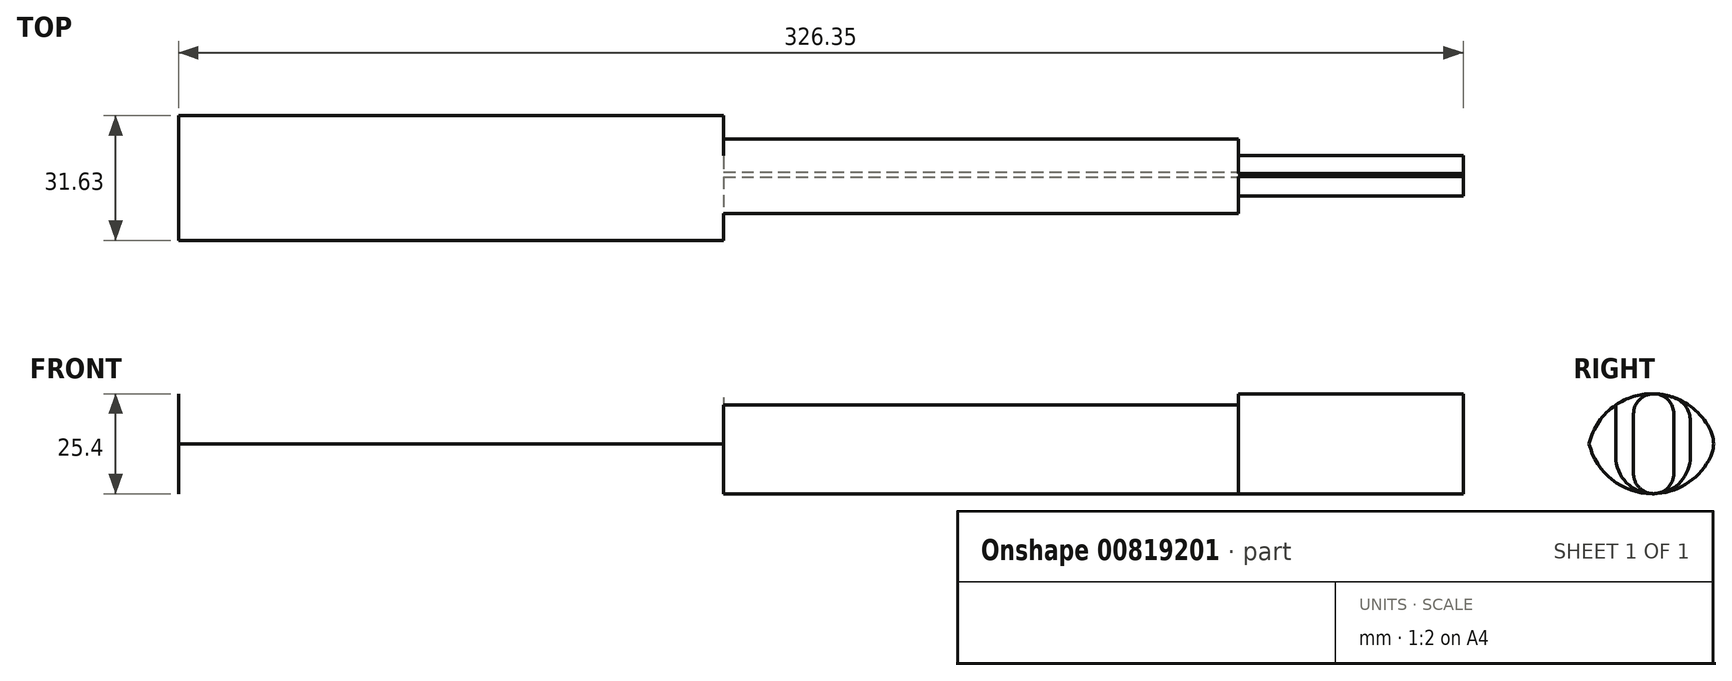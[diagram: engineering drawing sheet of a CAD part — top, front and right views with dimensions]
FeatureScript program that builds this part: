
annotation { "Feature Type Name" : "Feature", "Feature Type Description" : "" }
export const myFeature = defineFeature(function(context is Context, id is Id, definition is map)
    precondition{}
    {
        {
            var Q0;
            Q0=qCreatedBy(makeId("Top.planeOp"),FACE);
            var sketch = newSketch(context, id + "F0", { "sketchPlane" : qUnion([Q0])});
            skLineSegment(sketch, "E0.bottom", {"start": v(0, 0) * mm, "end": v(-138.51, 0) * mm});
            skLineSegment(sketch, "E0.top", {"start": v(0, -32.94) * mm, "end": v(-138.51, -32.94) * mm});
            skLineSegment(sketch, "E0.left", {"start": v(0, 0) * mm, "end": v(0, -32.94) * mm});
            skLineSegment(sketch, "E0.right", {"start": v(-138.51, 0) * mm, "end": v(-138.51, -32.94) * mm});
            skLineSegment(sketch, "E1.bottom", {"start": v(0, -6.77) * mm, "end": v(130.7, -6.77) * mm});
            skLineSegment(sketch, "E1.top", {"start": v(0, -25.72) * mm, "end": v(130.7, -25.72) * mm});
            skLineSegment(sketch, "E1.left", {"start": v(0, -6.77) * mm, "end": v(0, -25.72) * mm});
            skLineSegment(sketch, "E1.right", {"start": v(130.7, -6.77) * mm, "end": v(130.7, -25.72) * mm});
            skLineSegment(sketch, "E2.bottom", {"start": v(130.7, -10.98) * mm, "end": v(187.84, -10.98) * mm});
            skLineSegment(sketch, "E2.top", {"start": v(130.7, -21.2) * mm, "end": v(187.84, -21.2) * mm});
            skLineSegment(sketch, "E2.left", {"start": v(130.7, -10.98) * mm, "end": v(130.7, -21.2) * mm});
            skLineSegment(sketch, "E2.right", {"start": v(187.84, -10.98) * mm, "end": v(187.84, -21.2) * mm});
            skSolve(sketch);
        }
        {
            var Q0;
            Q0 = qSketchRegion(id + "F0", true);
            extrude(context, id + "F1", {"entities" : qUnion([Q0]), "oppositeDirection" : true, "depth" : 25.4 * mm, "offsetDistance" : 25.4 * mm});
        }
        {
            var Q0;
            Q0=makeQuery(id+"F1.opExtrude","CAP_EDGE",EDGE,{"disambiguationData":[OSD([sQuery(id+"F0.wireOp",EDGE,"E2.bottom")])],"isStart":true});
            var Q1;
            Q1=makeQuery(id+"F1.opExtrude","CAP_EDGE",EDGE,{"disambiguationData":[OSD([sQuery(id+"F0.wireOp",EDGE,"E2.top")])],"isStart":true});
            fillet(context, id + "F2", {"entities" : qUnion([Q0, Q1]), "radius" : 5.1 * mm, "tangentPropagation" : true, "allowEdgeOverflow" : false});
        }
        {
            var Q0;
            Q0=makeQuery(id+"F1.opExtrude","CAP_EDGE",EDGE,{"disambiguationData":[OSD([sQuery(id+"F0.wireOp",EDGE,"E1.bottom")])],"isStart":false});
            var Q1;
            Q1=makeQuery(id+"F1.opExtrude","CAP_EDGE",EDGE,{"disambiguationData":[OSD([sQuery(id+"F0.wireOp",EDGE,"E1.top")])],"isStart":false});
            fillet(context, id + "F3", {"entities" : qUnion([Q0, Q1]), "radius" : 9.4 * mm, "tangentPropagation" : true, "allowEdgeOverflow" : false});
        }
        {
            var Q0;
            Q0=makeQuery(id+"F1.opExtrude","CAP_EDGE",EDGE,{"disambiguationData":[OSD([sQuery(id+"F0.wireOp",EDGE,"E0.bottom")])],"isStart":true});
            var Q1;
            Q1=makeQuery(id+"F1.opExtrude","CAP_EDGE",EDGE,{"disambiguationData":[OSD([sQuery(id+"F0.wireOp",EDGE,"E0.top")])],"isStart":true});
            var Q2;
            Q2=makeQuery(id+"F1.opExtrude","CAP_EDGE",EDGE,{"disambiguationData":[OSD([sQuery(id+"F0.wireOp",EDGE,"E0.bottom")])],"isStart":false});
            var Q3;
            Q3=makeQuery(id+"F1.opExtrude","CAP_EDGE",EDGE,{"disambiguationData":[OSD([sQuery(id+"F0.wireOp",EDGE,"E0.top")])],"isStart":false});
            fillet(context, id + "F4", {"entities" : qUnion([Q0, Q1, Q2, Q3]), "radius" : 16.5 * mm, "tangentPropagation" : true, "allowEdgeOverflow" : false});
        }
        {
            var Q0;
            Q0=makeQuery(id+"F3.opFillet","BLEND_EDGE",EDGE,{"blendedFrom":[makeQuery(id+"F1.opExtrude","CAP_EDGE",EDGE,{"disambiguationData":[OSD([sQuery(id+"F0.wireOp",EDGE,"E1.bottom")])],"isStart":false}),makeQuery(id+"F1.opExtrude","SWEPT_FACE",FACE,{"disambiguationData":[OSD([sQuery(id+"F0.wireOp",EDGE,"E2.bottom")])]})],"blendedInto":[makeQuery(id+"F1.opExtrude","SWEPT_FACE",FACE,{"disambiguationData":[OSD([sQuery(id+"F0.wireOp",EDGE,"E2.bottom")])]})]});
            fillet(context, id + "F5", {"entities" : qUnion([Q0]), "radius" : 5.08 * mm, "tangentPropagation" : true, "allowEdgeOverflow" : false});
        }
        {
            var Q0;
            Q0=makeQuery(id+"F3.opFillet","BLEND_EDGE",EDGE,{"blendedFrom":[makeQuery(id+"F1.opExtrude","CAP_EDGE",EDGE,{"disambiguationData":[OSD([sQuery(id+"F0.wireOp",EDGE,"E1.top")])],"isStart":false}),makeQuery(id+"F1.opExtrude","SWEPT_FACE",FACE,{"disambiguationData":[OSD([sQuery(id+"F0.wireOp",EDGE,"E2.top")])]})],"blendedInto":[makeQuery(id+"F1.opExtrude","SWEPT_FACE",FACE,{"disambiguationData":[OSD([sQuery(id+"F0.wireOp",EDGE,"E2.top")])]})]});
            fillet(context, id + "F6", {"entities" : qUnion([Q0]), "radius" : 5.08 * mm, "tangentPropagation" : true, "allowEdgeOverflow" : false});
        }
        {
            var Q0;
            Q0=makeQuery(id+"F4.opFillet","BLEND_EDGE",EDGE,{"blendedFrom":[makeQuery(id+"F1.opExtrude","CAP_EDGE",EDGE,{"disambiguationData":[OSD([sQuery(id+"F0.wireOp",EDGE,"E0.bottom")])],"isStart":true}),makeQuery(id+"F1.opExtrude","SWEPT_FACE",FACE,{"disambiguationData":[OSD([sQuery(id+"F0.wireOp",EDGE,"E1.bottom")])]})],"blendedInto":[makeQuery(id+"F1.opExtrude","SWEPT_FACE",FACE,{"disambiguationData":[OSD([sQuery(id+"F0.wireOp",EDGE,"E1.bottom")])]})]});
            fillet(context, id + "F7", {"entities" : qUnion([Q0]), "radius" : 6.35 * mm, "tangentPropagation" : true, "allowEdgeOverflow" : false});
        }
        {
            var Q0;
            {var subQ0=sQuery(id+"F0.wireOp",EDGE,"E0.bottom");Q0=makeQuery(id+"F4.opFillet","BLEND_EDGE",EDGE,{"blendedFrom":[makeQuery(id+"F1.opExtrude","CAP_EDGE",EDGE,{"disambiguationData":[OSD([subQ0])],"isStart":true}),makeQuery(id+"F1.opExtrude","CAP_EDGE",EDGE,{"disambiguationData":[OSD([subQ0])],"isStart":false})],"blendedInto":[]});}
            fillet(context, id + "F8", {"entities" : qUnion([Q0]), "radius" : 7.62 * mm, "tangentPropagation" : true, "allowEdgeOverflow" : false});
        }
    });
